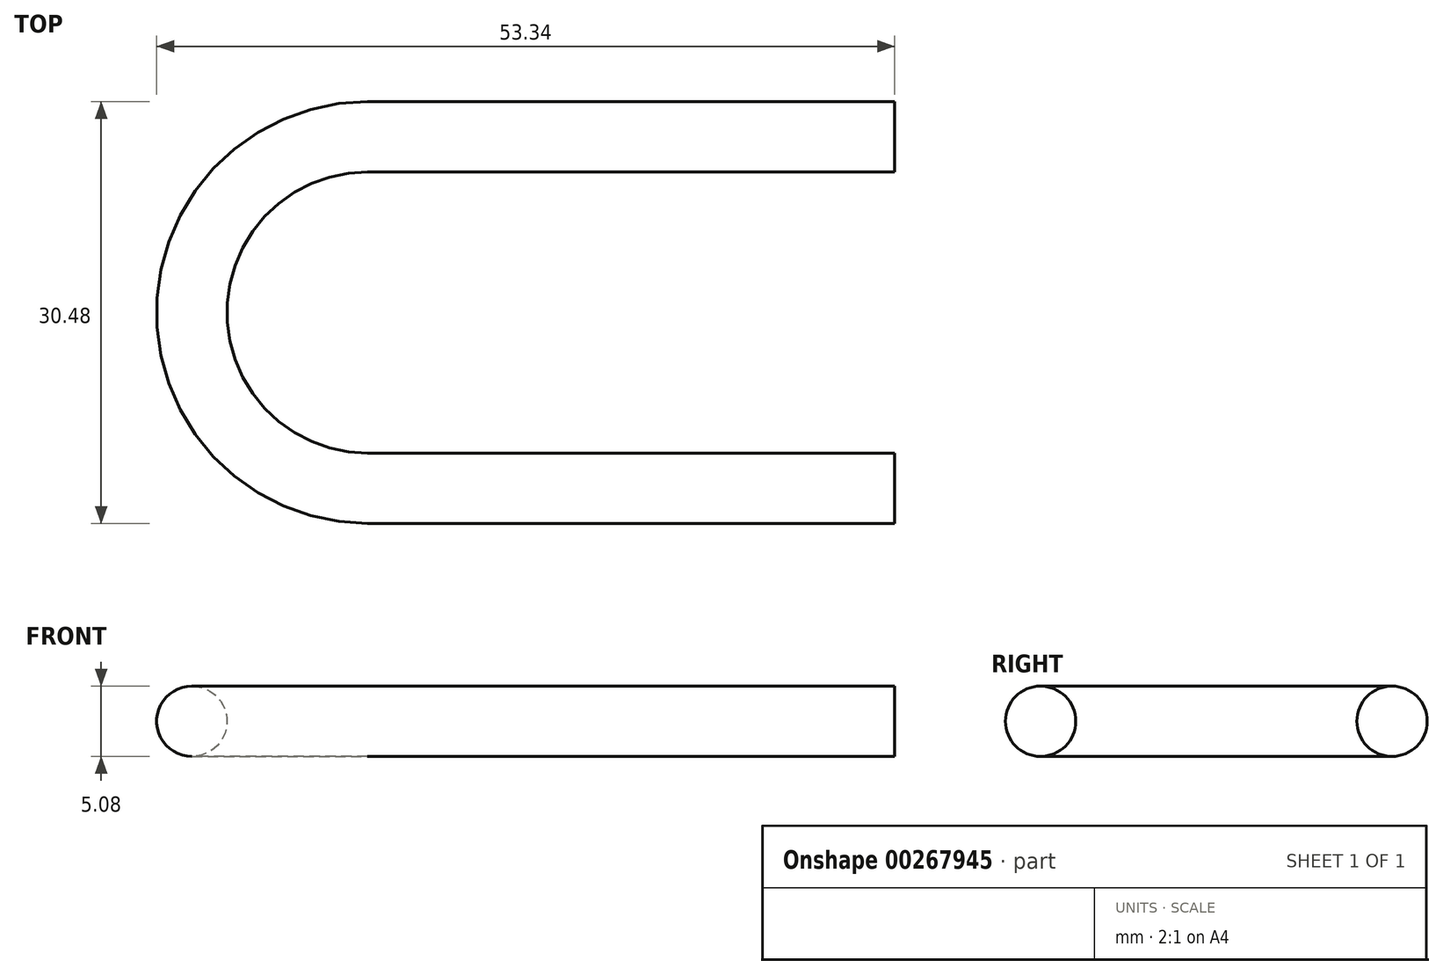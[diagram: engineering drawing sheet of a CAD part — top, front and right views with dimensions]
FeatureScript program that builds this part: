
annotation { "Feature Type Name" : "Feature", "Feature Type Description" : "" }
export const myFeature = defineFeature(function(context is Context, id is Id, definition is map)
    precondition{}
    {
        {
            var Q0;
            Q0=qCreatedBy(makeId("Top.planeOp"),FACE);
            var sketch = newSketch(context, id + "F0", { "sketchPlane" : qUnion([Q0])});
            skLineSegment(sketch, "E0.bottom", {"start": v(0, 25.4) * mm, "end": v(38.1, 25.4) * mm});
            skLineSegment(sketch, "E0.top", {"start": v(0, 0) * mm, "end": v(38.1, 0) * mm});
            skLineSegment(sketch, "E0.left", {"start": v(-12.7, 12.7) * mm, "end": v(-12.7, 12.7) * mm});
            skPoint(sketch, "E1.visualSharp", {"position": v(-12.7, 25.4) * mm});
            skArc(sketch, "E1.filletArc", {"start": v(0, 25.4) * mm, "mid": v(-8.98, 21.68) * mm, "end": v(-12.7, 12.7) * mm});
            skPoint(sketch, "E2.visualSharp", {"position": v(-12.7, 0) * mm});
            skArc(sketch, "E2.filletArc", {"start": v(-12.7, 12.7) * mm, "mid": v(-8.98, 3.72) * mm, "end": v(0, 0) * mm});
            skSolve(sketch);
        }
        {
            var Q0;
            Q0=qCreatedBy(makeId("Right.planeOp"),FACE);
            cPlane(context, id + "F1", {"entities" : qUnion([Q0]), "cplaneType" : CPlaneType.OFFSET, "offset" : 38.1 * mm, "width" : 152.4 * mm, "height" : 152.4 * mm});
        }
        {
            var Q0;
            Q0=qCreatedBy(id+"F1.planeOp",FACE);
            var sketch = newSketch(context, id + "F2", { "sketchPlane" : qUnion([Q0])});
            skCircle(sketch, "E3", {"center": v(0, 0) * mm, "radius": 2.54 * mm});
            skSolve(sketch);
        }
        {
            var Q0;
            Q0=makeQuery(id+"F2.imprint","IMPRINT",FACE,{"disambiguationData":[TD([[makeQuery(id+"F2.imprint","IMPRINT",EDGE,{"derivedFrom":sQuery(id+"F2.wireOp",EDGE,"E3")}),1.0]])]});
            var Q1;
            Q1=sQuery(id+"F0.wireOp",EDGE,"E0.bottom");
            var Q2;
            Q2=sQuery(id+"F0.wireOp",EDGE,"E1.filletArc");
            var Q3;
            Q3=sQuery(id+"F0.wireOp",EDGE,"E2.filletArc");
            var Q4;
            Q4=sQuery(id+"F0.wireOp",EDGE,"E0.top");
            sweep(context, id + "F3", {"profiles" : qUnion([Q0]), "path" : qUnion([Q1, Q2, Q3, Q4])});
        }
    });
